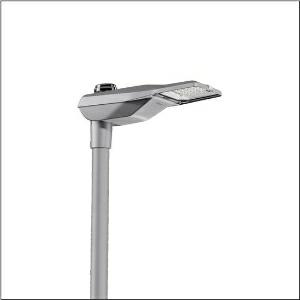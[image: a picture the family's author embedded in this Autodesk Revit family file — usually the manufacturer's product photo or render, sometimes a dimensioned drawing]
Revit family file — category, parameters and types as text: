
# Revit family: streetlight_sl_21_micro___st1_5a_5xe5p47n08cb_4c70
name_source: partatom
category: Lighting Fixtures
units: mm (PartAtom-declared; Revit-internal decimal feet)

## family parameters
Cut with Voids When Loaded = No
Host = Face
Light Source = No
Part Type = Normal
Room Calculation Point = No
Round Connector Dimension = Use Diameter
Shared = No

## types (1)
- --- (1 x LED, 2340 lm, 15.8 W, 4000K)
    Apparent Load = 16 VA
    CIE Flux Codes = 22 53 95 100 100
    Color Rendering = 70
    Color Temperature = 4000K
    Default Elevation = 1800 mm
    Description = Streetlight SL 21 micro, mast luminaire, primary light control with lens, of PMMA, primary optical cover: cover, of toughened safety glass, transparent, light distribution: ST1.5a, light emission: direct distribution, primary light characteristic: asymmetric, installation type: post-top, LED, 3G 1.5mm², High Power LED, rated luminous flux: 2.340lm, luminous efficacy: 148lm/W, light colour: 740, colour temperature: 4000K, control gear: NEMA (7pin), control: overheat protection, pre-setting: linear dimming characteristic, constant luminous flux control, time-dependent luminous flux control, flexible luminous flux parameterisation, mains connection: 230..240V, AC, 50/60Hz, connection cable pre-assembled, cable length: 6,5m, wiring characteristics: H07RN-F, start of lifetime: 16W, end of service life: 16W, reduction: 8W, luminaire housing, of diecast aluminium (EN AC-44300), powder-coated, Siteco® metallic grey (DB 702S), corrosivity category C5 mid according to DIN EN ISO 12944, multi-level sealing system, sealing non-destructively replaceable, inclination adjustable: 0°, 5°, 10°, 15°, length: 528mm, width: 235mm, height: 110mm, spigot size: 76/60mm (post-top), mounting height: 4..8m, protection rating (complete): IP66, insulation class (complete): insulation class I (protective earthing), certification: CE, ENEC, ENEC+, VDE, impact resistance: IK10, permissible operating ambient temperature for outdoor applications: -40..+50°C, standard-compliant lighting for roads and squares, packaging unit: 1 piece

Light Distribution: ST1.5a
    Height = 110 mm
    Lamp = 1 x LED
    Lamp Light Flux = 2340 lm
    Lamp Power = 15.8 W
    Lamp count = 1
    Length = 528 mm
    Luminous efficacy = 148 lm/W
    Manufacturer = Siteco
    ModVariant = No
    Model = 5XE5P47N08CB
    Number of Poles = 1
    OnlyDefault = Yes
    Power Factor = 1
    Product Name = Streetlight SL 21 micro | ST1.5a
    Product group = mast luminaire | pylon top
    ProductGroupID = 6100
    Protection Class = Protection class I
    Protection Degree = IP 66
    RLX_Detail_Level = 1
    RLX_Emergency_Light_Flux = 0 lm
    RLX_Emergency_Type = 0
    RLX_Emergency_Type_DB = No
    RlxData = <blob elided: 102157 chars, md5=fbad56ea>
    Socket = socket
    Standby Power = 0 W
    System Light Flux = 2340 lm
    System Power = 16 W
    Type Comments = factory setting: luminous flux: 100 % | dim-lin: 254 | 300 mA
    Type Image = l_1294375.jpg
    URL = http://relux.com
    VarID = @adj_133734
    Voltage = 0 V
    Weight = 0.00 kg
    Width = 235 mm

## geometry (parser evidence)
native form markers: Blend x4, Sweep x12
no freeform markers — native parametric forms only
